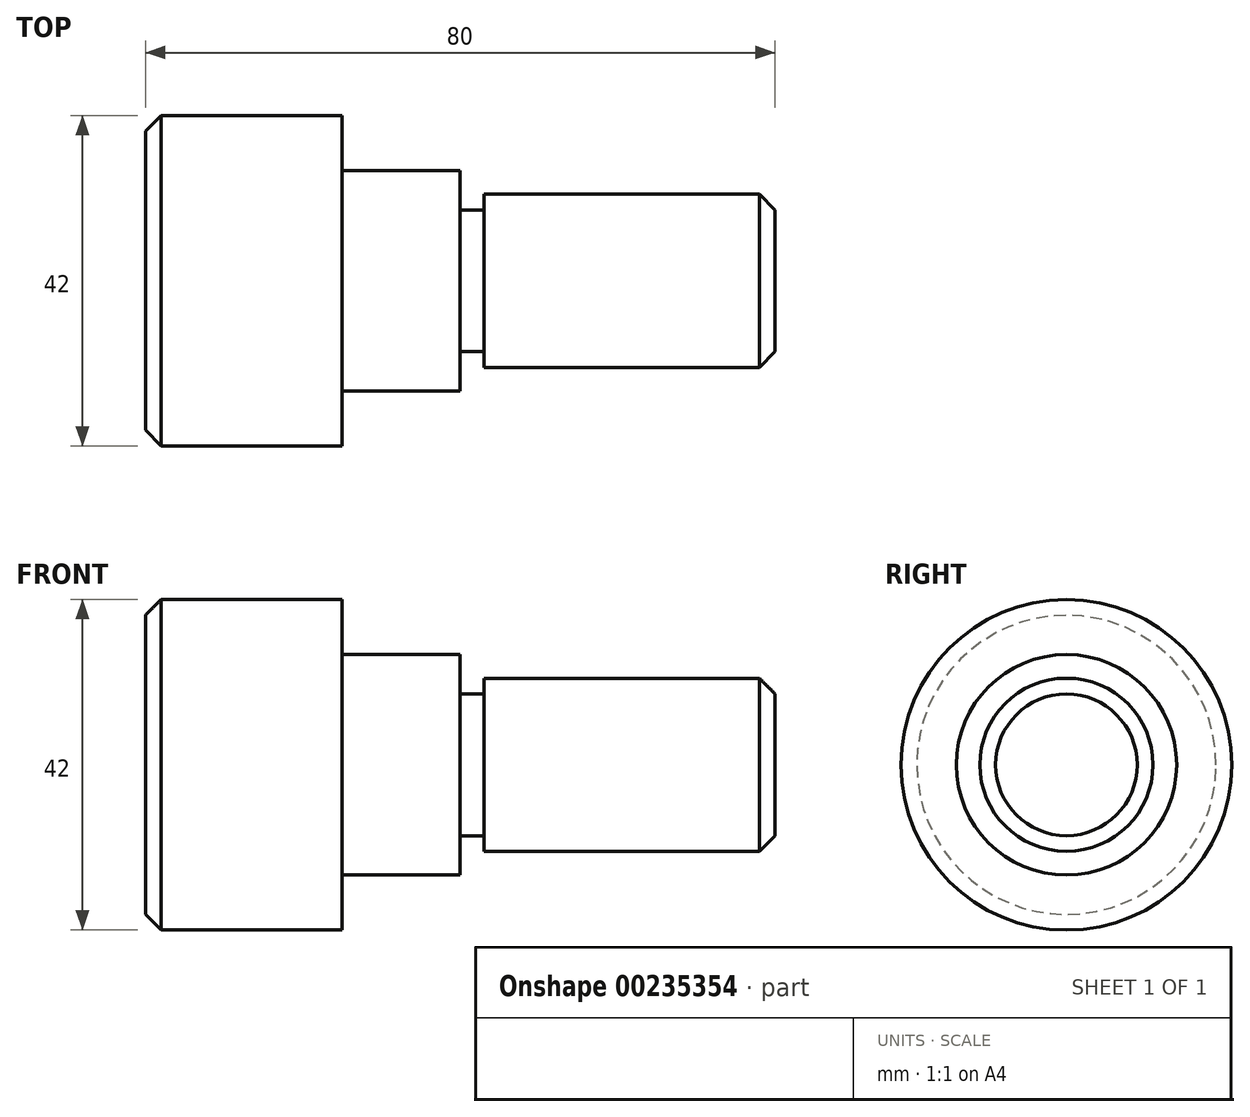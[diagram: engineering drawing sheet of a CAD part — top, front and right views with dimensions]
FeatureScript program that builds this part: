
annotation { "Feature Type Name" : "Feature", "Feature Type Description" : "" }
export const myFeature = defineFeature(function(context is Context, id is Id, definition is map)
    precondition{}
    {
        {
            var Q0;
            Q0=qCreatedBy(makeId("Front.planeOp"),FACE);
            var sketch = newSketch(context, id + "F0", { "sketchPlane" : qUnion([Q0])});
            skLineSegment(sketch, "E0", {"start": v(-35.7, 21) * mm, "end": v(-37.7, 19) * mm});
            skLineSegment(sketch, "E1", {"start": v(-37.7, 19) * mm, "end": v(-37.7, 0) * mm});
            skLineSegment(sketch, "E2", {"start": v(-37.7, 0) * mm, "end": v(-35.7, 0) * mm});
            skLineSegment(sketch, "E3", {"start": v(-35.7, 0) * mm, "end": v(-35.7, 21) * mm});
            skLineSegment(sketch, "E4", {"start": v(-35.7, 21) * mm, "end": v(-12.7, 21) * mm});
            skLineSegment(sketch, "E5", {"start": v(-12.7, 21) * mm, "end": v(-12.7, 0) * mm});
            skLineSegment(sketch, "E6", {"start": v(-12.7, 0) * mm, "end": v(-35.7, 0) * mm});
            skLineSegment(sketch, "E7", {"start": v(-12.7, 14) * mm, "end": v(2.3, 14) * mm});
            skLineSegment(sketch, "E8", {"start": v(2.3, 14) * mm, "end": v(2.3, 0) * mm});
            skLineSegment(sketch, "E9", {"start": v(2.3, 0) * mm, "end": v(-12.7, 0) * mm});
            skLineSegment(sketch, "E10", {"start": v(2.3, 9) * mm, "end": v(5.3, 9) * mm});
            skLineSegment(sketch, "E11", {"start": v(5.3, 9) * mm, "end": v(5.3, 0) * mm});
            skLineSegment(sketch, "E12", {"start": v(5.3, 0) * mm, "end": v(2.3, 0) * mm});
            skLineSegment(sketch, "E13", {"start": v(5.3, 9) * mm, "end": v(5.3, 11) * mm});
            skLineSegment(sketch, "E14", {"start": v(5.3, 11) * mm, "end": v(40.3, 11) * mm});
            skLineSegment(sketch, "E15", {"start": v(40.3, 11) * mm, "end": v(40.3, 0) * mm});
            skLineSegment(sketch, "E16", {"start": v(40.3, 0) * mm, "end": v(5.3, 0) * mm});
            skLineSegment(sketch, "E17", {"start": v(40.3, 11) * mm, "end": v(42.3, 9) * mm});
            skLineSegment(sketch, "E18", {"start": v(42.3, 9) * mm, "end": v(42.3, 0) * mm});
            skLineSegment(sketch, "E19", {"start": v(42.3, 0) * mm, "end": v(40.3, 0) * mm});
            skLineSegment(sketch, "E20", {"start": v(-51.67, 0) * mm, "end": v(110.23, 0) * mm, "construction": true});
            skSolve(sketch);
        }
        {
            var Q0;
            Q0 = qSketchRegion(id + "F0", true);
            var Q1;
            Q1=sQuery(id+"F0.wireOp",EDGE,"E20");
            revolve(context, id + "F1", {"entities" : qUnion([Q0]), "axis" : qUnion([Q1]), "revolveType" : RevolveType.FULL});
        }
    });
